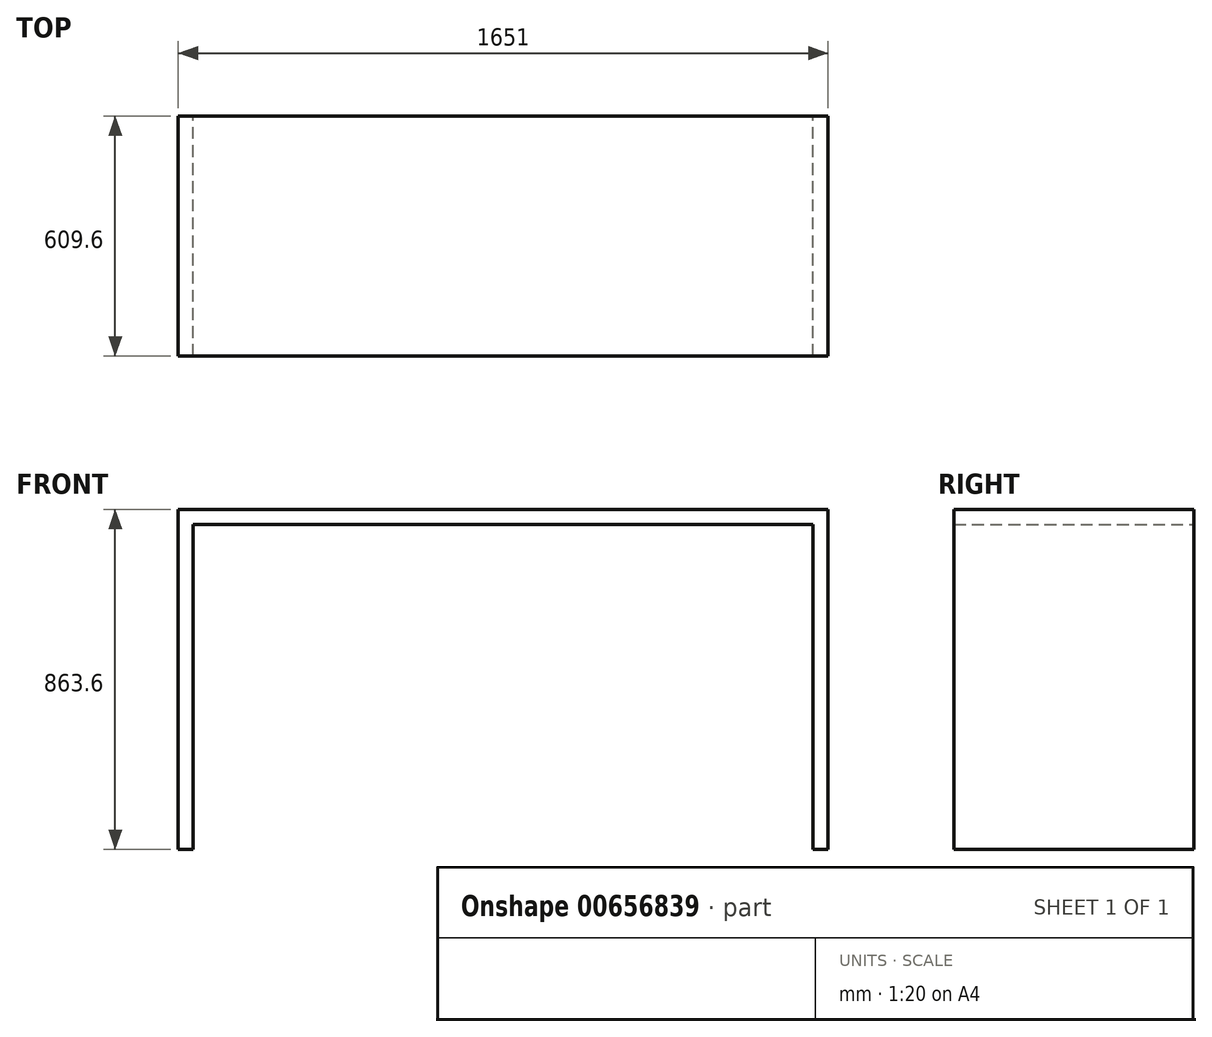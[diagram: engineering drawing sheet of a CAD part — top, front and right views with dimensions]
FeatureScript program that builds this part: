
annotation { "Feature Type Name" : "Feature", "Feature Type Description" : "" }
export const myFeature = defineFeature(function(context is Context, id is Id, definition is map)
    precondition{}
    {
        {
            var Q0;
            Q0=qCreatedBy(makeId("Front.planeOp"),FACE);
            var sketch = newSketch(context, id + "F0", { "sketchPlane" : qUnion([Q0])});
            skLineSegment(sketch, "E0.bottom", {"start": v(-1651, 863.6) * mm, "end": v(0, 863.6) * mm});
            skLineSegment(sketch, "E0.top", {"start": v(-1651, 0) * mm, "end": v(-1612.9, 0) * mm});
            skLineSegment(sketch, "E0.left", {"start": v(-1651, 863.6) * mm, "end": v(-1651, 0) * mm});
            skLineSegment(sketch, "E0.right", {"start": v(0, 863.6) * mm, "end": v(0, 0) * mm});
            skLineSegment(sketch, "E1.0", {"start": v(-1612.9, 825.5) * mm, "end": v(-38.1, 825.5) * mm});
            skLineSegment(sketch, "E2.0", {"start": v(-38.1, 825.5) * mm, "end": v(-38.1, 0) * mm});
            skLineSegment(sketch, "E3.0", {"start": v(-1612.9, 825.5) * mm, "end": v(-1612.9, 0) * mm});
            skLineSegment(sketch, "E4.trimOffspring", {"start": v(-38.1, 0) * mm, "end": v(0, 0) * mm});
            skSolve(sketch);
        }
        {
            var Q0;
            Q0 = qSketchRegion(id + "F0", true);
            extrude(context, id + "F1", {"entities" : qUnion([Q0]), "depth" : 609.6 * mm, "offsetDistance" : 25.4 * mm});
        }
    });
